# Revit family: TEMID_Турникет-трипод_TS1000 Pro
name_source: partatom
category: Электрооборудование
units: mm (PartAtom-declared; Revit-internal decimal feet)

## family parameters
Всегда вертикально = Нет
На основе рабочей плоскости = Нет
Общий = Да
При загрузке вырезать с полостями = Нет
Размер круглого соединителя = Использовать диаметр
Тип детали = Другая панель
Точка расчета площади = Нет

## types (1)
- TS1000 Pro
    ADSK_Группирование = 3. Периферийное оборудование
    ADSK_Единица измерения = шт.
    ADSK_Завод-изготовитель = TEMID
    ADSK_Количество = 1
    ADSK_Количество фаз = 1
    ADSK_Коэффициент мощности = 0.95
    ADSK_Марка = TS1000 Pro
    ADSK_Наименование = Турникет-трипод. Корпус из нержавеющей стали.  Индикатор разрешенного направления прохода. Планки «антипаника», вход для кнопки аварийной разблокировки. Рабочая температура -28°C - +60°C. Р. Питание: AC 220В/110А,. Размеры: 520?980?280мм, длина преграждающих планок - 500 мм. Вес - 34 кг.
    ADSK_Напряжение = 220 В
    ADSK_Номинальная мощность = 120 Вт
    ADSK_Полная мощность = 114 В·А
    ADSK_Размер_Высота = 990 мм
    ADSK_Размер_Глубина = 600 мм
    ADSK_Размер_Ширина = 310 мм
    ADSK_Тип = TS1000 Pro
    ADSK_Ток = 1 А
    URL = https://temid-global.ru
    Материал = Серый
    Отметка по умолчанию = 0 мм
